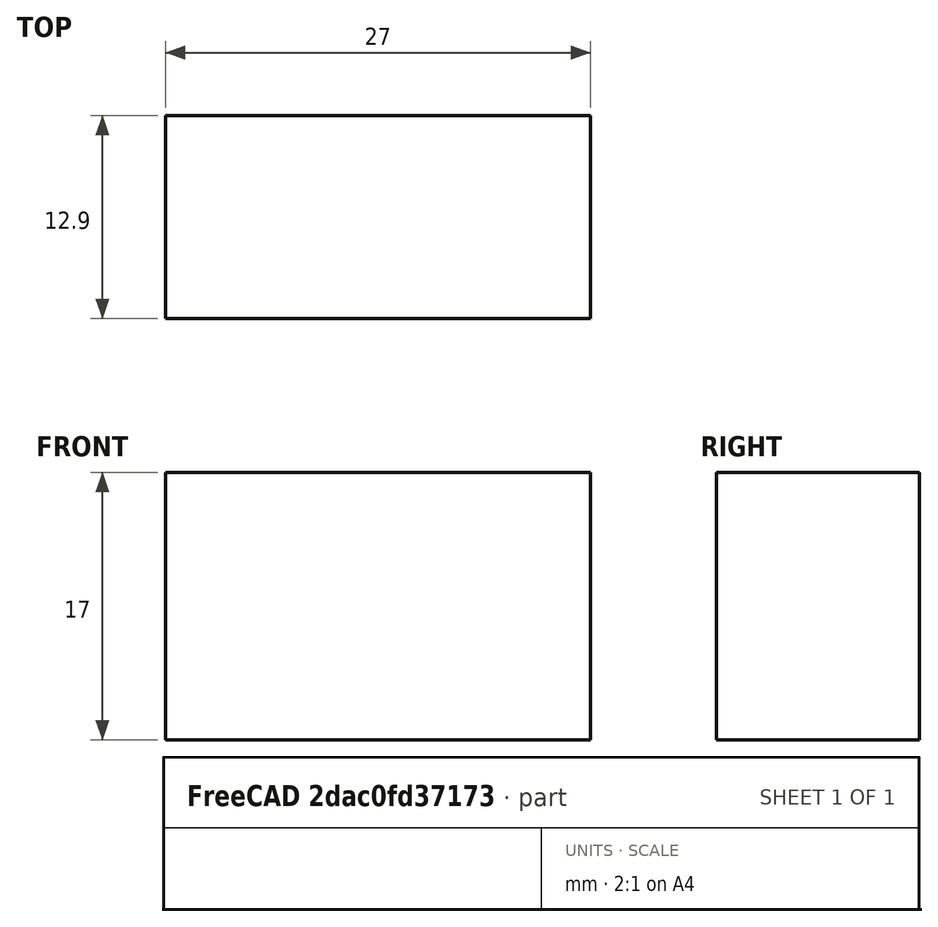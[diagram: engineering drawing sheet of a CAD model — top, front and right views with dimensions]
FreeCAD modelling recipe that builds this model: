
FCSTD DOCUMENT  (FreeCAD 1.0R39319 (Git))
Label: buck_circuit
License: All rights reserved
LicenseURL: http://en.wikipedia.org/wiki/All_rights_reserved
objects: Spreadsheet::Sheet×1, Sketcher::SketchObject×1, PartDesign::Pad×1, PartDesign::Body×1
note: 6 computed .brp shape members not serialized (recipe doc carries the construction recipe); baked Part::Feature solids carry a one-line shape summary decoded from their .brp

FEATURE [Spreadsheet::Sheet] Spreadsheet
  cells = A2='length; B2(length)=62; A3='width; B3(width)=27
FEATURE [Sketcher::SketchObject] Sketch
  ArcFitTolerance = 1e-06
  AttachmentSupport = -> [XY_Plane]
  FullyConstrained = true
  MakeInternals = false
  MapMode = 5
  expr: Constraints[9] = Spreadsheet.width
  sketch-geometry (4):
    g0: LineSegment StartX=20 StartY=22.9 StartZ=0 EndX=20 EndY=10 EndZ=0
    g1: LineSegment StartX=20 StartY=10 StartZ=0 EndX=47 EndY=10 EndZ=0
    g2: LineSegment StartX=47 StartY=10 StartZ=0 EndX=47 EndY=22.9 EndZ=0
    g3: LineSegment StartX=47 StartY=22.9 StartZ=0 EndX=20 EndY=22.9 EndZ=0
  constraints (12):
    c: Coincident(g0,g1)
    c: Coincident(g1,g2)
    c: Coincident(g2,g3)
    c: Coincident(g3,g0)
    c: Vertical(g0)
    c: Vertical(g2)
    c: Horizontal(g1)
    c: Horizontal(g3)
    c: DistanceY(g0,g0) = 12.9
    c: DistanceX(g0,g1) = 27
    c: DistanceY(g-1,g0) = 10
    c: DistanceX(g-1,g0) = 20
FEATURE [PartDesign::Pad] Pad
  Direction = (0,0,1)
  Length = 17
  Length2 = 10
  Profile = -> Sketch
  ReferenceAxis = -> Sketch [N_Axis]
  Suppressed = false
  Type = 0
FEATURE [PartDesign::Body] Body
  AllowCompound = false
  Group = -> [Sketch,Pad]
  Origin = -> Origin
  Tip = -> Pad
